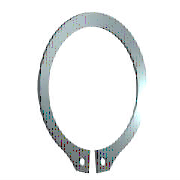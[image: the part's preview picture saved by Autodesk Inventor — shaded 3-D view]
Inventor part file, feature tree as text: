
AUTODESK INVENTOR PART (.ipt)
format: ipt  version: 2020 (Build 240168000, 168)  size: 155,648 bytes
history: native  units: mm (DEFAULTED — no unit token found)
features: extrude x1, other x1, plane x1
ambient origin geometry x8: Origin, YZ Plane, XZ Plane, XY Plane, X Axis, Y Axis, Z Axis, Center Point
bodies: Solid1 (feature_tree)
feature tree (3):
  extrude  "轴承体"  Depth=65.5mm
  other  "Work Axis1"
  plane  "Work Plane1"
